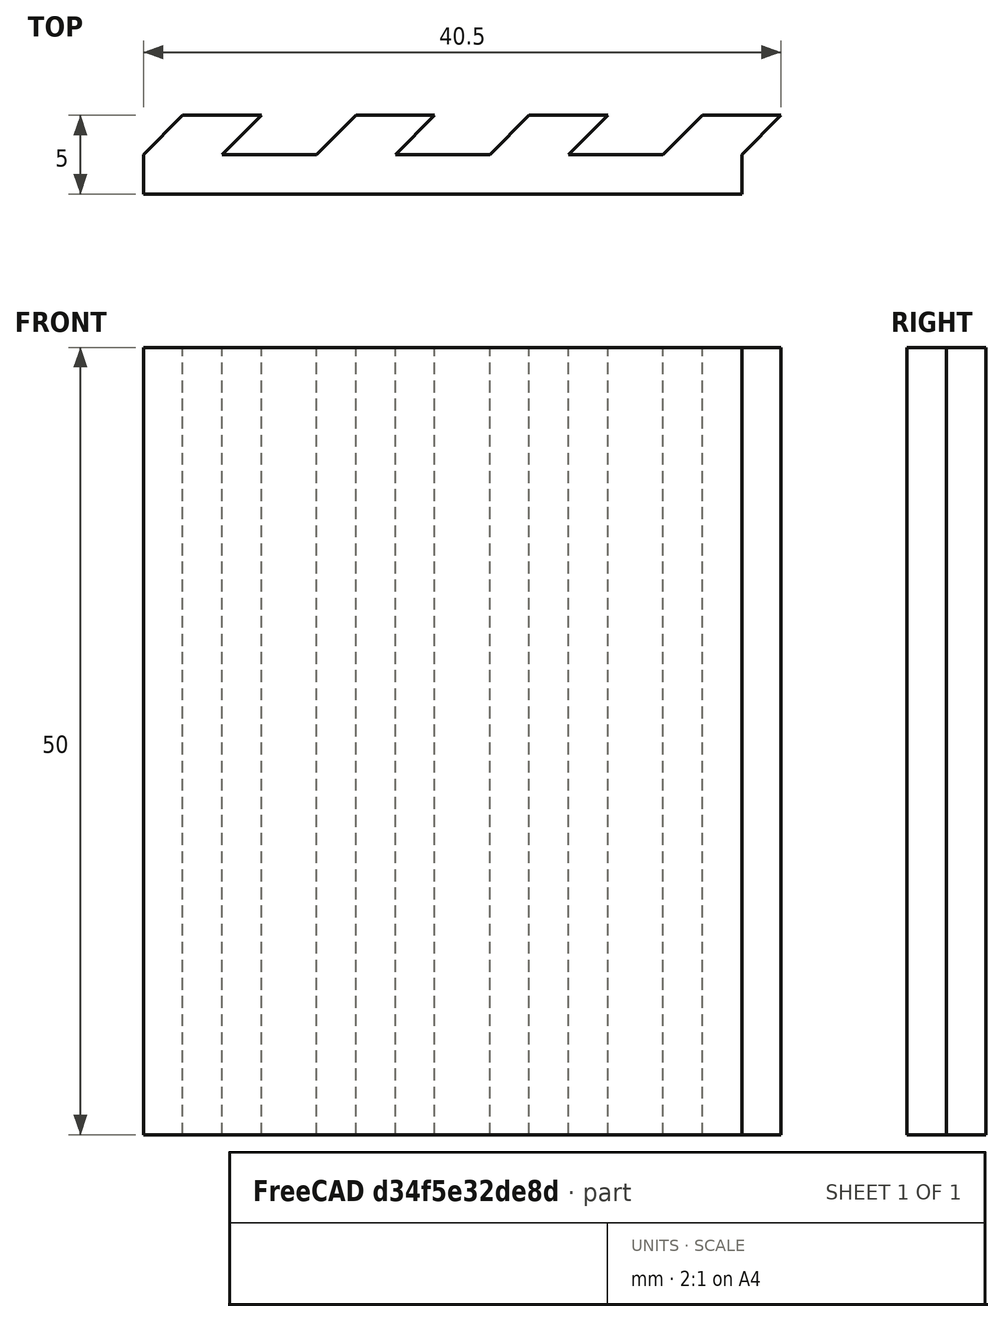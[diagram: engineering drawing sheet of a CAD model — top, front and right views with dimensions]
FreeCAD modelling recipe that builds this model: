
FCSTD DOCUMENT  (FreeCAD 1.0R39109 (Git))
Label: RevK75WallMount
License: All rights reserved
LicenseURL: https://en.wikipedia.org/wiki/All_rights_reserved
objects: Sketcher::SketchObject×1, PartDesign::Pad×1, PartDesign::Body×1
note: 6 computed .brp shape members not serialized (recipe doc carries the construction recipe); baked Part::Feature solids carry a one-line shape summary decoded from their .brp

FEATURE [Sketcher::SketchObject] Sketch
  ArcFitTolerance = 1e-06
  AttachmentSupport = -> [XY_Plane]
  FullyConstrained = true
  MakeInternals = false
  MapMode = 5
  sketch-geometry (20):
    g0: LineSegment StartX=0 StartY=0 StartZ=0 EndX=38 EndY=0 EndZ=0
    g1: LineSegment StartX=38 StartY=0 StartZ=0 EndX=38 EndY=2.5 EndZ=0
    g2: LineSegment StartX=38 StartY=2.5 StartZ=0 EndX=40.5 EndY=5 EndZ=0
    g3: LineSegment StartX=40.5 StartY=5 StartZ=0 EndX=35.5 EndY=5 EndZ=0
    g4: LineSegment StartX=35.5 StartY=5 StartZ=0 EndX=33 EndY=2.5 EndZ=0
    g5: LineSegment StartX=33 StartY=2.5 StartZ=0 EndX=27 EndY=2.5 EndZ=0
    g6: LineSegment StartX=27 StartY=2.5 StartZ=0 EndX=29.5 EndY=5 EndZ=0
    g7: LineSegment StartX=29.5 StartY=5 StartZ=0 EndX=24.5 EndY=5 EndZ=0
    g8: LineSegment StartX=24.5 StartY=5 StartZ=0 EndX=22 EndY=2.5 EndZ=0
    g9: LineSegment StartX=22 StartY=2.5 StartZ=0 EndX=16 EndY=2.5 EndZ=0
    g10: LineSegment StartX=16 StartY=2.5 StartZ=0 EndX=18.5 EndY=5 EndZ=0
    g11: LineSegment StartX=18.5 StartY=5 StartZ=0 EndX=13.5 EndY=5 EndZ=0
    g12: LineSegment StartX=13.5 StartY=5 StartZ=0 EndX=11 EndY=2.5 EndZ=0
    g13: LineSegment StartX=11 StartY=2.5 StartZ=0 EndX=5 EndY=2.5 EndZ=0
    g14: LineSegment StartX=5 StartY=2.5 StartZ=0 EndX=7.5 EndY=5 EndZ=0
    g15: LineSegment StartX=7.5 StartY=5 StartZ=0 EndX=2.5 EndY=5 EndZ=0
    g16: LineSegment StartX=2.5 StartY=5 StartZ=0 EndX=0 EndY=2.5 EndZ=0
    g17: LineSegment StartX=0 StartY=2.5 StartZ=0 EndX=0 EndY=0 EndZ=0
    g18: LineSegment [constr] StartX=0 StartY=5 StartZ=0 EndX=60 EndY=5 EndZ=0
    g19: LineSegment [constr] StartX=0 StartY=2.5 StartZ=0 EndX=60 EndY=2.5 EndZ=0
  constraints (62):
    c: Coincident(g-1,g0)
    c: Horizontal(g0)
    c: Coincident(g0,g1)
    c: Vertical(g1)
    c: Coincident(g1,g2)
    c: Coincident(g2,g3)
    c: Horizontal(g3)
    c: Coincident(g3,g4)
    c: Coincident(g4,g5)
    c: Horizontal(g5)
    c: Coincident(g5,g6)
    c: Coincident(g6,g7)
    c: Horizontal(g7)
    c: Coincident(g7,g8)
    c: Coincident(g8,g9)
    c: Horizontal(g9)
    c: Coincident(g9,g10)
    c: Coincident(g10,g11)
    c: Horizontal(g11)
    c: Coincident(g11,g12)
    c: Coincident(g12,g13)
    c: Horizontal(g13)
    c: Coincident(g13,g14)
    c: Coincident(g14,g15)
    c: Horizontal(g15)
    c: Coincident(g15,g16)
    c: PointOnObject(g16,g-2)
    c: Coincident(g16,g17)
    c: PointOnObject(g17,g-1)
    c: Vertical(g17)
    c: Horizontal(g18)
    c: Horizontal(g19)
    c: PointOnObject(g15,g18)
    c: PointOnObject(g11,g18)
    c: PointOnObject(g7,g18)
    c: PointOnObject(g3,g18)
    c: PointOnObject(g16,g19)
    c: PointOnObject(g13,g19)
    c: PointOnObject(g9,g19)
    c: PointOnObject(g5,g19)
    c: PointOnObject(g1,g19)
    c: Angle(g13,g14) = 0.785398
    c: Angle(g9,g10) = 0.785398
    c: Angle(g5,g6) = 0.785398
    c: Angle(g19,g2) = 0.785398
    c: Parallel(g16,g14)
    c: Parallel(g12,g10)
    c: Parallel(g8,g6)
    c: Parallel(g4,g2)
    c: DistanceX(g15,g15) = 5
    c: DistanceX(g11,g11) = 5
    c: DistanceX(g7,g7) = 5
    c: DistanceX(g3,g3) = 5
    c: Distance(g-1,g19) = 2.5
    c: PointOnObject(g19,g-2)
    c: PointOnObject(g18,g-2)
    c: Distance(g18,g-1) = 5
    c: DistanceX(g13,g13) = 6
    c: DistanceX(g9,g9) = 6
    c: DistanceX(g5,g5) = 6
    c: DistanceX(g18,g19) = 0
    c: DistanceX(g19,g19) = 60
FEATURE [PartDesign::Pad] Pad
  Direction = (0,0,1)
  Length = 50
  Length2 = 10
  Profile = -> Sketch
  ReferenceAxis = -> Sketch [N_Axis]
  Refine = true
  Suppressed = false
  Type = 0
FEATURE [PartDesign::Body] Body  label="WallMount"
  AllowCompound = false
  Group = -> [Sketch,Pad]
  Origin = -> Origin
  Tip = -> Pad
